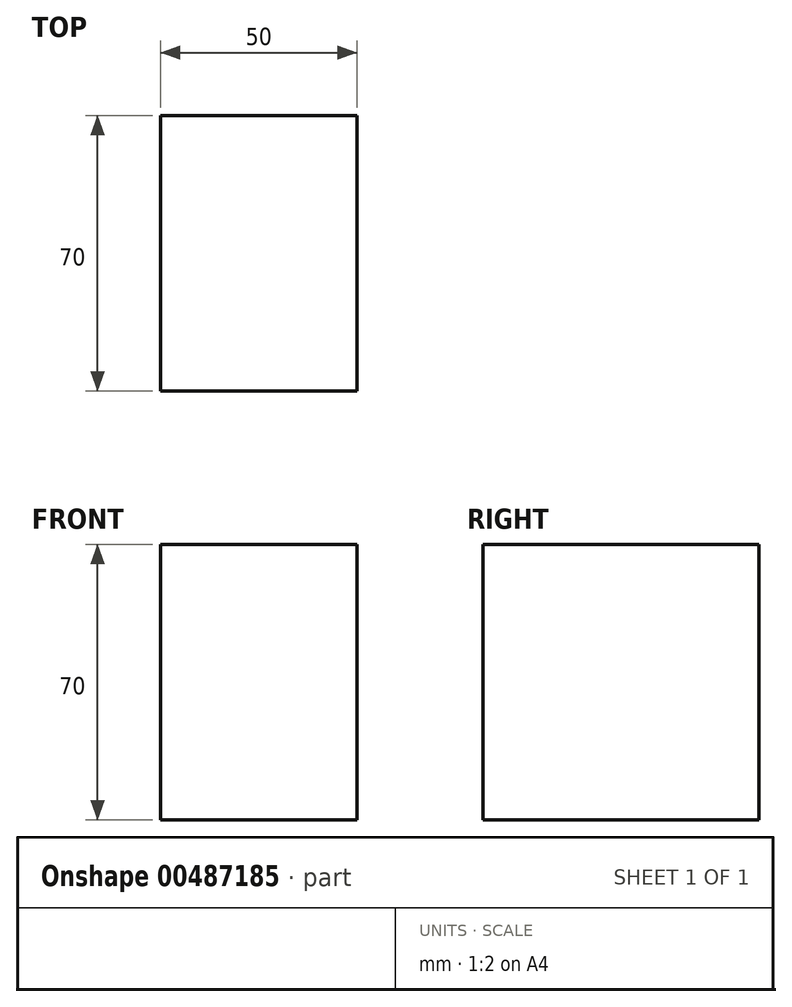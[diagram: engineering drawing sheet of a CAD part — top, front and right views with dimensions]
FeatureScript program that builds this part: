
annotation { "Feature Type Name" : "Feature", "Feature Type Description" : "" }
export const myFeature = defineFeature(function(context is Context, id is Id, definition is map)
    precondition{}
    {
        {
            var Q0;
            Q0=qCreatedBy(makeId("Top.planeOp"),FACE);
            var sketch = newSketch(context, id + "F0", { "sketchPlane" : qUnion([Q0])});
            skLineSegment(sketch, "E0.bottom", {"start": v(25, 35) * mm, "end": v(-25, 35) * mm});
            skLineSegment(sketch, "E0.top", {"start": v(25, -35) * mm, "end": v(-25, -35) * mm});
            skLineSegment(sketch, "E0.left", {"start": v(25, 35) * mm, "end": v(25, -35) * mm});
            skLineSegment(sketch, "E0.right", {"start": v(-25, 35) * mm, "end": v(-25, -35) * mm});
            skPoint(sketch, "E0.middle", {"position": v(0, 0) * mm});
            skSolve(sketch);
        }
        {
            var Q0;
            Q0=makeQuery(id+"F0.imprint","IMPRINT",FACE,{"disambiguationData":[TD([[makeQuery(id+"F0.imprint","IMPRINT",EDGE,{"derivedFrom":sQuery(id+"F0.wireOp",EDGE,"E0.bottom")}),1.0]])]});
            extrude(context, id + "F1", {"entities" : qUnion([Q0]), "depth" : 70 * mm});
        }
    });
